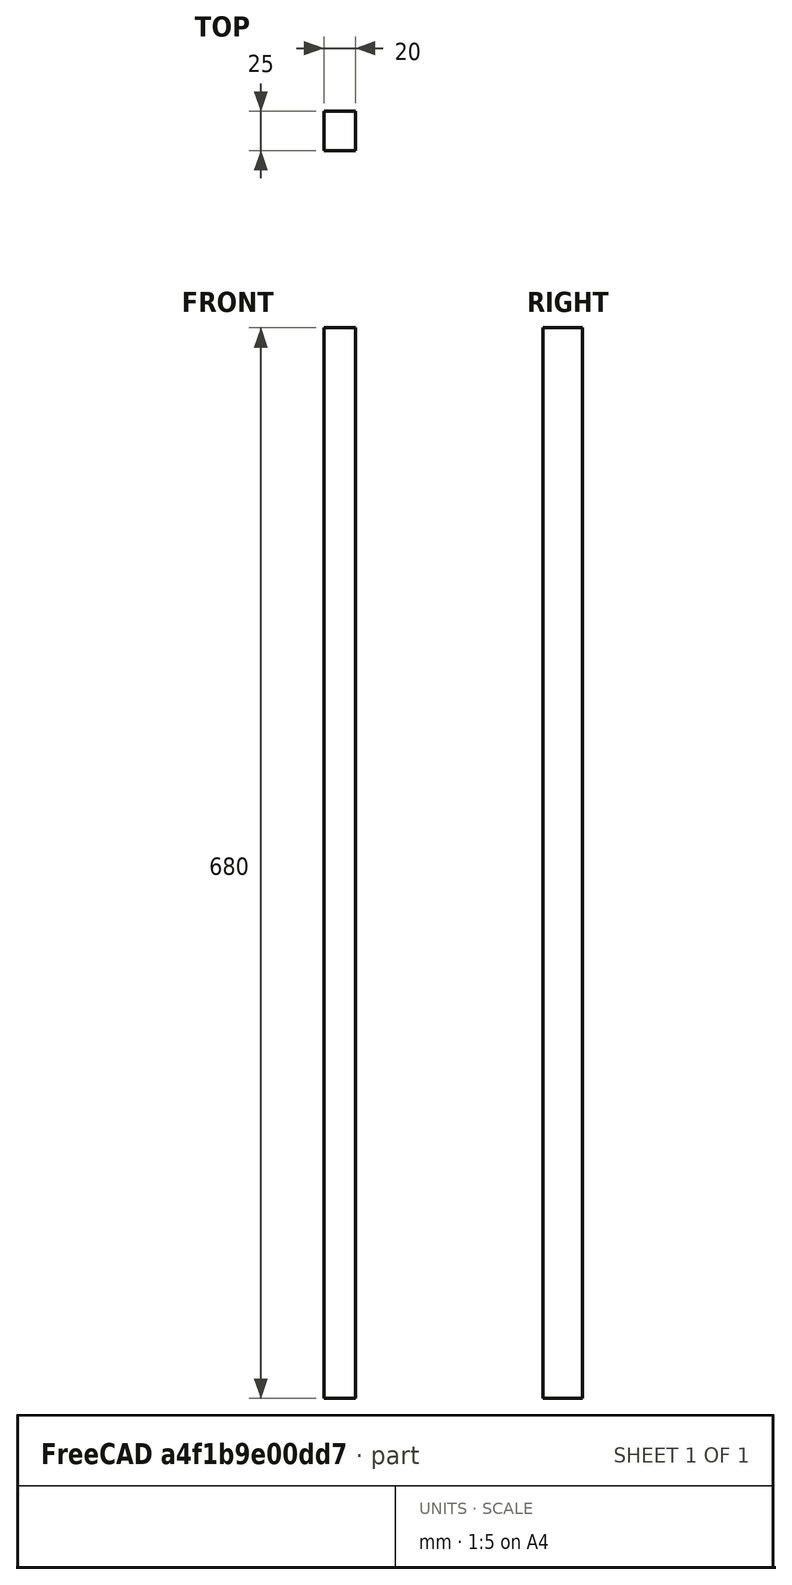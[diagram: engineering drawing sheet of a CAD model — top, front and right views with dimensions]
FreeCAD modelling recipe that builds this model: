
FCSTD DOCUMENT  (FreeCAD 0.21R33771 (Git))
Label: right_bed_rail
License: All rights reserved
LicenseURL: http://en.wikipedia.org/wiki/All_rights_reserved
objects: Sketcher::SketchObject×1, PartDesign::Pad×1, PartDesign::Body×1
note: 4 computed .brp shape members not serialized (recipe doc carries the construction recipe); baked Part::Feature solids carry a one-line shape summary decoded from their .brp

FEATURE [Sketcher::SketchObject] Sketch002
  FullyConstrained = true
  MapMode = 5
  Support = -> [XY_Plane002]
  sketch-geometry (4):
    g0: LineSegment StartX=125 StartY=85 StartZ=0 EndX=145 EndY=85 EndZ=0
    g1: LineSegment StartX=145 StartY=85 StartZ=0 EndX=145 EndY=60 EndZ=0
    g2: LineSegment StartX=145 StartY=60 StartZ=0 EndX=125 EndY=60 EndZ=0
    g3: LineSegment StartX=125 StartY=60 StartZ=0 EndX=125 EndY=85 EndZ=0
  constraints (12):
    c: Coincident(g0,g1)
    c: Coincident(g1,g2)
    c: Coincident(g2,g3)
    c: Coincident(g3,g0)
    c: Horizontal(g0)
    c: Horizontal(g2)
    c: Vertical(g1)
    c: Vertical(g3)
    c: DistanceX(g2,g2) = 20
    c: Distance(g2,g-2) = 125
    c: DistanceY(g-1,g2) = 60
    c: Distance(g0,g2) = 25
FEATURE [PartDesign::Pad] Pad002
  Direction = (0,0,1)
  Length = 680
  Length2 = 10
  Profile = -> Sketch002
  ReferenceAxis = -> Sketch002 [N_Axis]
  Type = 0
FEATURE [PartDesign::Body] Body002  label="bed right rail"
  Group = -> [Sketch002,Pad002]
  Origin = -> Origin002
  Tip = -> Pad002
